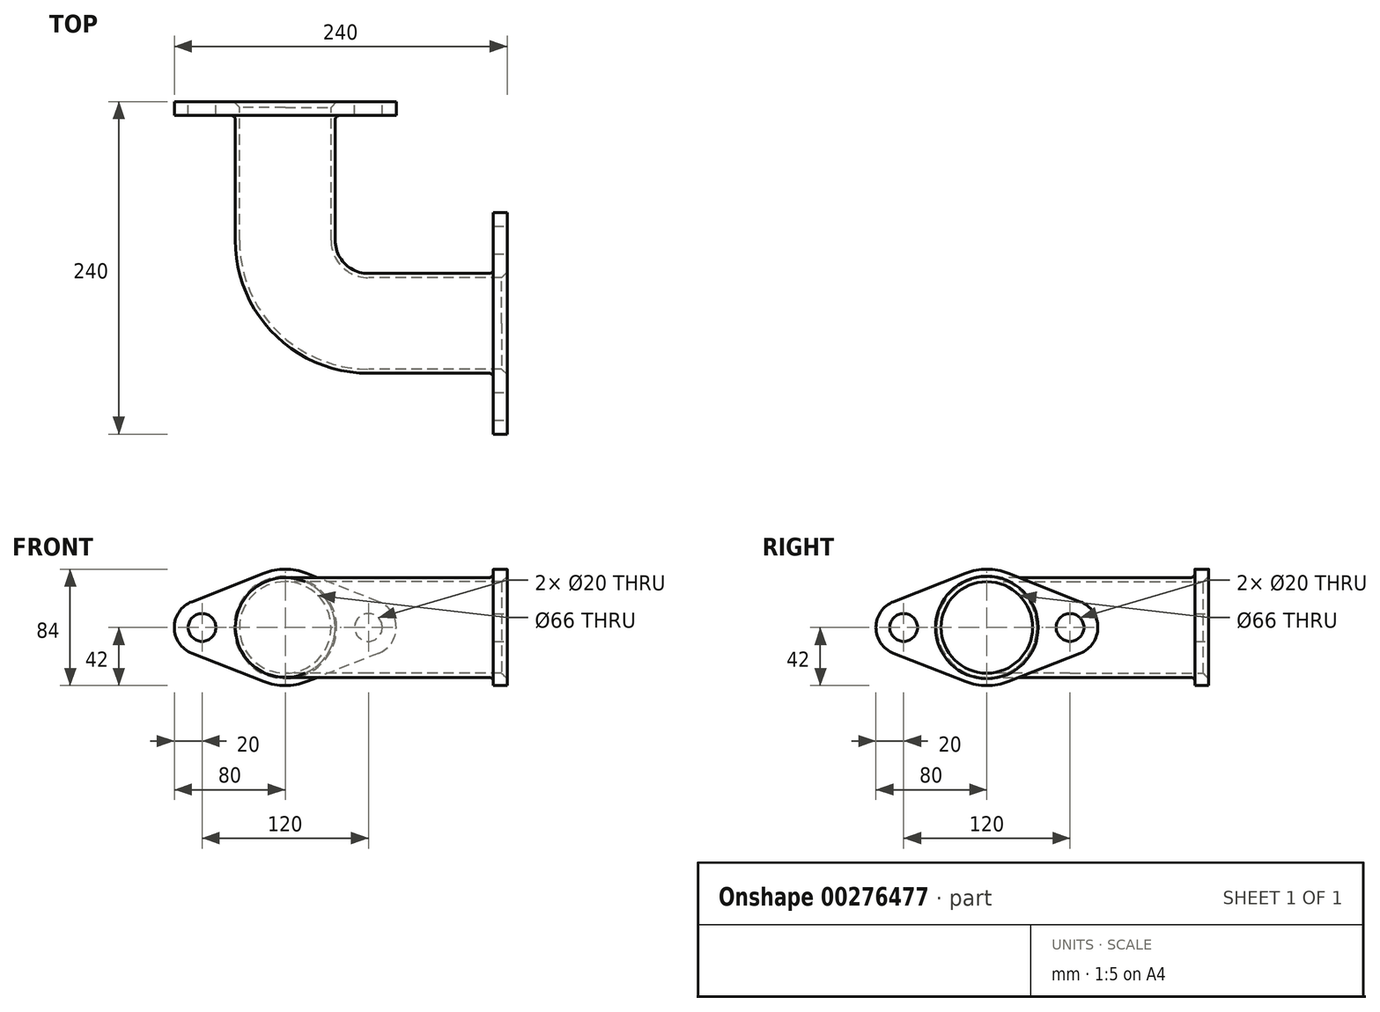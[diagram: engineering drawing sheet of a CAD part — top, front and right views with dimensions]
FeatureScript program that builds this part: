
annotation { "Feature Type Name" : "Feature", "Feature Type Description" : "" }
export const myFeature = defineFeature(function(context is Context, id is Id, definition is map)
    precondition{}
    {
        {
            var Q0;
            Q0=qCreatedBy(makeId("Top.planeOp"),FACE);
            var sketch = newSketch(context, id + "F0", { "sketchPlane" : qUnion([Q0])});
            skArc(sketch, "E0", {"start": v(-60, 0) * mm, "mid": v(-42.43, -42.43) * mm, "end": v(0, -60) * mm});
            skLineSegment(sketch, "E1", {"start": v(-60, 0) * mm, "end": v(-60, 100) * mm});
            skLineSegment(sketch, "E2", {"start": v(0, -60) * mm, "end": v(100, -60) * mm});
            skSolve(sketch);
        }
        {
            var Q0;
            Q0=qCreatedBy(makeId("Right.planeOp"),FACE);
            var Q1;
            Q1=sQuery(id+"F0.wireOp",VERTEX,"E2.end");
            cPlane(context, id + "F1", {"entities" : qUnion([Q0, Q1]), "cplaneType" : CPlaneType.PLANE_POINT, "offset" : 25 * mm, "width" : 150 * mm, "height" : 150 * mm});
        }
        {
            var Q0;
            Q0=qCreatedBy(id+"F1.planeOp",FACE);
            var sketch = newSketch(context, id + "F2", { "sketchPlane" : qUnion([Q0])});
            skPoint(sketch, "E3.0", {"position": v(-60, 0) * mm});
            skCircle(sketch, "E4", {"center": v(-60, 0) * mm, "radius": 36 * mm});
            skSolve(sketch);
        }
        {
            var Q0;
            Q0=makeQuery(id+"F2.imprint","IMPRINT",FACE,{"disambiguationData":[TD([[makeQuery(id+"F2.imprint","IMPRINT",EDGE,{"derivedFrom":sQuery(id+"F2.wireOp",EDGE,"E4")}),1.0]])]});
            var Q1;
            Q1=sQuery(id+"F0.wireOp",EDGE,"E2");
            var Q2;
            Q2=sQuery(id+"F0.wireOp",EDGE,"E0");
            var Q3;
            Q3=sQuery(id+"F0.wireOp",EDGE,"E1");
            sweep(context, id + "F3", {"profiles" : qUnion([Q0]), "path" : qUnion([Q1, Q2, Q3])});
        }
        {
            var Q0;
            Q0=makeQuery(id+"F3.opSweep","CAP_FACE",FACE,{"disambiguationData":[OSD([sQuery(id+"F0.wireOp",VERTEX,"E1.end"),sQuery(id+"F2.wireOp",EDGE,"E4")])],"isStart":false});
            var Q1;
            Q1=makeQuery(id+"F3.opSweep","CAP_FACE",FACE,{"disambiguationData":[OSD([sQuery(id+"F0.wireOp",VERTEX,"E2.end"),sQuery(id+"F2.wireOp",EDGE,"E4")])],"isStart":true});
            shell(context, id + "F4", {"entities" : qUnion([Q0, Q1]), "thickness" : 3 * mm});
        }
        {
            var Q0;
            Q0=qCreatedBy(id+"F1.planeOp",FACE);
            var sketch = newSketch(context, id + "F5", { "sketchPlane" : qUnion([Q0])});
            skCircle(sketch, "E5.0", {"center": v(-60, 0) * mm, "radius": 33 * mm});
            skArc(sketch, "E6", {"start": v(-75.4, -39.07) * mm, "mid": v(-60, -42) * mm, "end": v(-44.6, -39.07) * mm});
            skLineSegment(sketch, "E7", {"start": v(-60, 0) * mm, "end": v(-120, 0) * mm, "construction": true});
            skLineSegment(sketch, "E8", {"start": v(-60, 0) * mm, "end": v(0, 0) * mm, "construction": true});
            skArc(sketch, "E9", {"start": v(-127.33, 18.6) * mm, "mid": v(-140, 0) * mm, "end": v(-127.33, -18.6) * mm});
            skCircle(sketch, "E10", {"center": v(-120, 0) * mm, "radius": 10 * mm});
            skLineSegment(sketch, "E11", {"start": v(-127.33, -18.6) * mm, "end": v(-75.4, -39.07) * mm});
            skLineSegment(sketch, "E12.MirrorCS", {"start": v(-127.33, 18.6) * mm, "end": v(-75.4, 39.07) * mm});
            skLineSegment(sketch, "E13", {"start": v(-60, 0) * mm, "end": v(-60, 13.55) * mm, "construction": true});
            skCircle(sketch, "E14.MirrorC", {"center": v(0, 0) * mm, "radius": 10 * mm});
            skLineSegment(sketch, "E15.MirrorCS", {"start": v(7.33, 18.6) * mm, "end": v(-44.6, 39.07) * mm});
            skArc(sketch, "E16.MirrorCS", {"start": v(7.33, 18.6) * mm, "mid": v(20, 0) * mm, "end": v(7.33, -18.6) * mm});
            skLineSegment(sketch, "E17.MirrorCS", {"start": v(7.33, -18.6) * mm, "end": v(-44.6, -39.07) * mm});
            skArc(sketch, "E18.trimOffspring", {"start": v(-44.6, 39.07) * mm, "mid": v(-60, 42) * mm, "end": v(-75.4, 39.07) * mm});
            skSolve(sketch);
        }
        {
            var Q0;
            Q0=makeQuery(id+"F5.imprint","IMPRINT",FACE,{"disambiguationData":[TD([[makeQuery(id+"F5.imprint","IMPRINT",EDGE,{"derivedFrom":sQuery(id+"F5.wireOp",EDGE,"E5.0")}),-1.0]])]});
            extrude(context, id + "F6", {"entities" : qUnion([Q0]), "operationType" : NewBodyOperationType.ADD, "oppositeDirection" : true, "depth" : 10 * mm});
        }
        {
            var Q0;
            Q0=makeQuery(id+"F4.opShell","OFFSET_EDGE",EDGE,{"disambiguationData":[OSD([sQuery(id+"F0.wireOp",VERTEX,"E2.end"),sQuery(id+"F2.wireOp",EDGE,"E4")])]});
            chamfer(context, id + "F7", {"entities" : qUnion([Q0]), "width" : 4 * mm, "tangentPropagation" : true});
        }
        {
            var Q0;
            Q0=makeQuery(id+"F6.boolean.opBoolean","INTERSECT",EDGE,{"derivedFrom":[makeQuery(id+"F3.opSweep","SWEPT_FACE",FACE,{"disambiguationData":[OSD([sQuery(id+"F0.wireOp",EDGE,"E2"),sQuery(id+"F2.wireOp",EDGE,"E4")])]}),makeQuery(id+"F6.opExtrude","CAP_FACE",FACE,{"disambiguationData":[OSD([sQuery(id+"F5.wireOp",EDGE,"E5.0"),sQuery(id+"F5.wireOp",EDGE,"E6"),sQuery(id+"F5.wireOp",EDGE,"E9"),sQuery(id+"F5.wireOp",EDGE,"E10"),sQuery(id+"F5.wireOp",EDGE,"E11"),sQuery(id+"F5.wireOp",EDGE,"E12.MirrorCS"),sQuery(id+"F5.wireOp",EDGE,"E14.MirrorC"),sQuery(id+"F5.wireOp",EDGE,"E15.MirrorCS"),sQuery(id+"F5.wireOp",EDGE,"E16.MirrorCS"),sQuery(id+"F5.wireOp",EDGE,"E17.MirrorCS"),sQuery(id+"F5.wireOp",EDGE,"E18.trimOffspring")])],"isStart":false})]});
            fillet(context, id + "F8", {"entities" : qUnion([Q0]), "radius" : 3 * mm, "tangentPropagation" : true, "allowEdgeOverflow" : false});
        }
        {
            var Q0;
            Q0=makeQuery(id+"F3.opSweep","CAP_FACE",FACE,{"disambiguationData":[OSD([sQuery(id+"F0.wireOp",VERTEX,"E1.end"),sQuery(id+"F2.wireOp",EDGE,"E4")])],"isStart":false});
            cPlane(context, id + "F9", {"entities" : qUnion([Q0]), "cplaneType" : CPlaneType.OFFSET, "offset" : 0 * mm, "width" : 150 * mm, "height" : 150 * mm});
        }
        {
            var Q0;
            Q0=qCreatedBy(id+"F9.planeOp",FACE);
            var sketch = newSketch(context, id + "F10", { "sketchPlane" : qUnion([Q0])});
            skArc(sketch, "E19", {"start": v(44.6, -39.07) * mm, "mid": v(60, -42) * mm, "end": v(75.4, -39.07) * mm});
            skLineSegment(sketch, "E20", {"start": v(60, 0) * mm, "end": v(0, 0) * mm, "construction": true});
            skLineSegment(sketch, "E21", {"start": v(60, 0) * mm, "end": v(120, 0) * mm, "construction": true});
            skArc(sketch, "E22", {"start": v(-7.33, 18.6) * mm, "mid": v(-20, 0) * mm, "end": v(-7.33, -18.6) * mm});
            skCircle(sketch, "E23", {"center": v(0, 0) * mm, "radius": 10 * mm});
            skLineSegment(sketch, "E24", {"start": v(-7.33, -18.6) * mm, "end": v(44.6, -39.07) * mm});
            skLineSegment(sketch, "E25.MirrorCS", {"start": v(-7.33, 18.6) * mm, "end": v(44.6, 39.07) * mm});
            skLineSegment(sketch, "E26", {"start": v(60, 0) * mm, "end": v(60, 13.07) * mm, "construction": true});
            skCircle(sketch, "E27.MirrorC", {"center": v(120, 0) * mm, "radius": 10 * mm});
            skLineSegment(sketch, "E28.MirrorCS", {"start": v(127.33, 18.6) * mm, "end": v(75.4, 39.07) * mm});
            skArc(sketch, "E29.MirrorCS", {"start": v(127.33, 18.6) * mm, "mid": v(140, 0) * mm, "end": v(127.33, -18.6) * mm});
            skLineSegment(sketch, "E30.MirrorCS", {"start": v(127.33, -18.6) * mm, "end": v(75.4, -39.07) * mm});
            skArc(sketch, "E31.trimOffspring", {"start": v(75.4, 39.07) * mm, "mid": v(60, 42) * mm, "end": v(44.6, 39.07) * mm});
            skCircle(sketch, "E32.0", {"center": v(60, 0) * mm, "radius": 33 * mm});
            skSolve(sketch);
        }
        {
            var Q0;
            Q0=makeQuery(id+"F10.imprint","IMPRINT",FACE,{"disambiguationData":[TD([[makeQuery(id+"F10.imprint","IMPRINT",EDGE,{"derivedFrom":sQuery(id+"F10.wireOp",EDGE,"1c2f95a4-de3f-4344-ae2f-6508c9c8e7e5.0")}),-1.0]])]});
            var Q1;
            Q1=makeQuery(id+"F10.imprint","IMPRINT",FACE,{"disambiguationData":[TD([[makeQuery(id+"F10.imprint","IMPRINT",EDGE,{"derivedFrom":sQuery(id+"F10.wireOp",EDGE,"E19")}),1.0]])]});
            extrude(context, id + "F11", {"entities" : qUnion([Q0, Q1]), "operationType" : NewBodyOperationType.ADD, "oppositeDirection" : true, "depth" : 10 * mm});
        }
        {
            var Q0;
            Q0=makeQuery(id+"F4.opShell","OFFSET_EDGE",EDGE,{"disambiguationData":[OSD([sQuery(id+"F0.wireOp",VERTEX,"E1.end"),sQuery(id+"F2.wireOp",EDGE,"E4")])]});
            chamfer(context, id + "F12", {"entities" : qUnion([Q0]), "width" : 4 * mm, "tangentPropagation" : true});
        }
        {
            var Q0;
            Q0=makeQuery(id+"F11.boolean.opBoolean","INTERSECT",EDGE,{"derivedFrom":[makeQuery(id+"F3.opSweep","SWEPT_FACE",FACE,{"disambiguationData":[OSD([sQuery(id+"F0.wireOp",EDGE,"E1"),sQuery(id+"F2.wireOp",EDGE,"E4")])]}),makeQuery(id+"F11.opExtrude","CAP_FACE",FACE,{"disambiguationData":[OSD([sQuery(id+"F10.wireOp",EDGE,"E19"),sQuery(id+"F10.wireOp",EDGE,"E22"),sQuery(id+"F10.wireOp",EDGE,"E23"),sQuery(id+"F10.wireOp",EDGE,"E24"),sQuery(id+"F10.wireOp",EDGE,"E25.MirrorCS"),sQuery(id+"F10.wireOp",EDGE,"E27.MirrorC"),sQuery(id+"F10.wireOp",EDGE,"E28.MirrorCS"),sQuery(id+"F10.wireOp",EDGE,"E29.MirrorCS"),sQuery(id+"F10.wireOp",EDGE,"E30.MirrorCS"),sQuery(id+"F10.wireOp",EDGE,"E31.trimOffspring"),sQuery(id+"F10.wireOp",EDGE,"E32.0")])],"isStart":false})]});
            fillet(context, id + "F13", {"entities" : qUnion([Q0]), "radius" : 3 * mm, "tangentPropagation" : true, "allowEdgeOverflow" : false});
        }
    });
